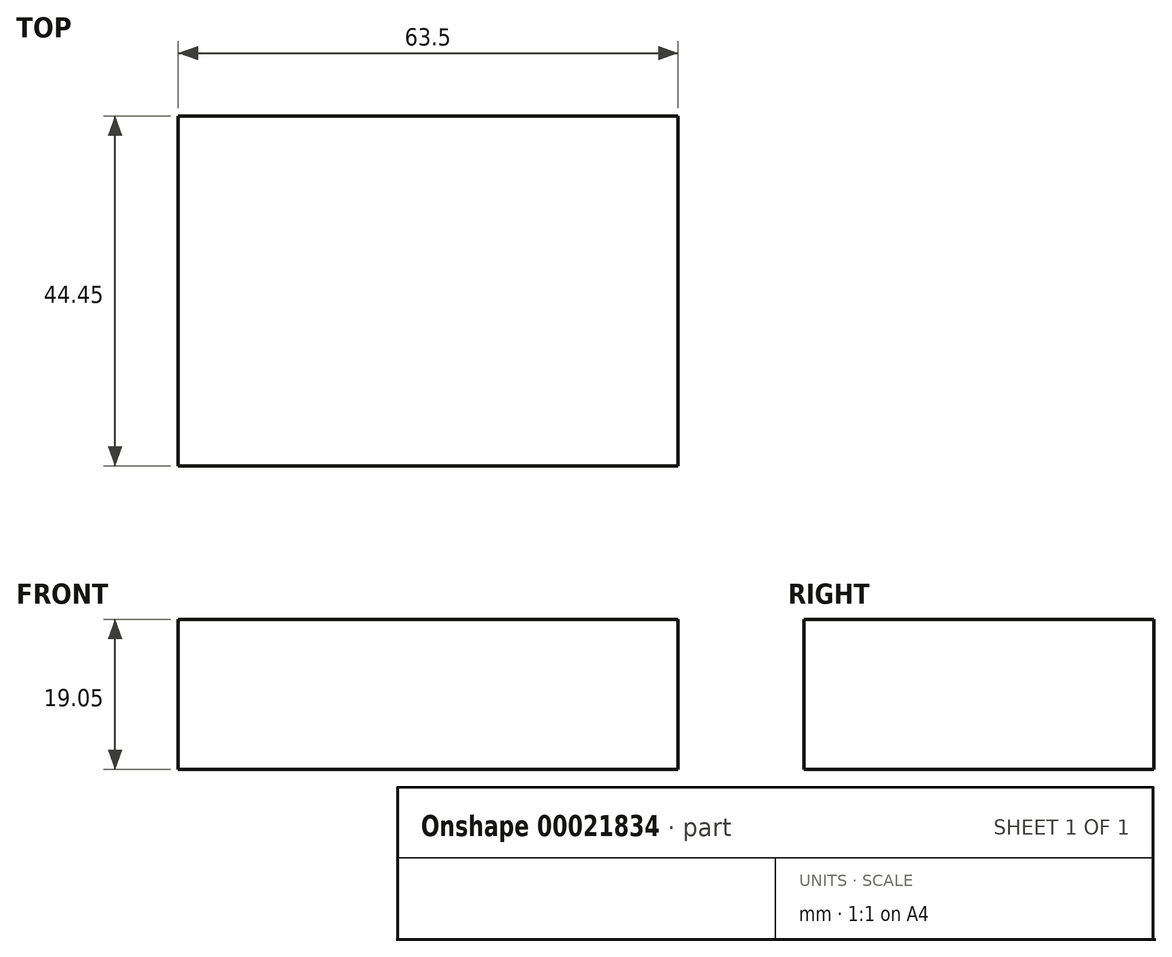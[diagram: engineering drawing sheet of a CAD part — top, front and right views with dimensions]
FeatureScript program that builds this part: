
annotation { "Feature Type Name" : "Feature", "Feature Type Description" : "" }
export const myFeature = defineFeature(function(context is Context, id is Id, definition is map)
    precondition{}
    {
        {
            var Q0;
            Q0=qCreatedBy(makeId("Top.planeOp"),FACE);
            var sketch = newSketch(context, id + "F0", { "sketchPlane" : qUnion([Q0])});
            skLineSegment(sketch, "E0.bottom", {"start": v(-21.6, 32.86) * mm, "end": v(41.9, 32.86) * mm});
            skLineSegment(sketch, "E0.top", {"start": v(-21.6, -11.6) * mm, "end": v(41.9, -11.6) * mm});
            skLineSegment(sketch, "E0.left", {"start": v(-21.6, 32.86) * mm, "end": v(-21.6, -11.6) * mm});
            skLineSegment(sketch, "E0.right", {"start": v(41.9, 32.86) * mm, "end": v(41.9, -11.6) * mm});
            skSolve(sketch);
        }
        {
            var Q0;
            Q0=makeQuery(id+"F0.imprint","IMPRINT",FACE,{"disambiguationData":[TD([[makeQuery(id+"F0.imprint","IMPRINT",EDGE,{"derivedFrom":sQuery(id+"F0.wireOp",EDGE,"E0.bottom")}),-1.0]])]});
            extrude(context, id + "F1", {"entities" : qUnion([Q0]), "depth" : 19.05 * mm});
        }
    });
